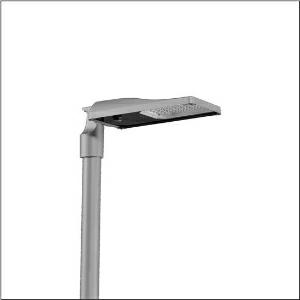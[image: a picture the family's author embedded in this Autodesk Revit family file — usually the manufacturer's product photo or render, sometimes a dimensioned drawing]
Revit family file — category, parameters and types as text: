
# Revit family: streetlight_sl_31_mini___st1_0a_5xh2d31r08ha_940f
name_source: partatom
category: Lighting Fixtures
units: mm (PartAtom-declared; Revit-internal decimal feet)

## family parameters
Cut with Voids When Loaded = No
Host = Face
Light Source = No
Part Type = Normal
Room Calculation Point = No
Round Connector Dimension = Use Diameter
Shared = No

## types (1)
- --- (1 x LED, 9230 lm, 68.3 W, 3000K)
    Apparent Load = 68 VA
    CIE Flux Codes = 37 72 97 100 100
    Color Rendering = 70
    Color Temperature = 3000K
    Default Elevation = 1800 mm
    Description = Streetlight SL 31 mini D4i, Desk-Remote mast luminaire for post-top, side-entry; light control with lens of PMMA; light distribution: ST1.0a, direct asymmetric distribution, for standard-compliant lighting for roads and squares; LED: luminous flux: 9.230lm, light colour: 730, colour temperature: 3000K; luminous efficacy: 135,1lm/W; control: pre-setting: logarithmic dimming characteristic, flexible luminous flux parameterisation, time-dependent luminous flux control, constant luminous flux control, power reduction, intelligent temperature release in ECG and LED module, overheat protection; luminaire housing, of diecast aluminium, Siteco® metallic grey (DB 702S), corrosivity category C5 high according to DIN EN ISO 12944; cover of toughened safety glass, transparent, mast flange of diecast aluminium, Siteco® metallic grey (DB 702S), spigot size: 76/60mm, mast flange included unmounted; with cable H07RN-F 2x 1.5mm², cable length: 8,5m, connection cable pre-assembled; mains connection: 220..240V, AC, 50/60Hz; power consumption (at start of service life): 68,3W / (at end of service life): 74,5W / (with reduced operation 50%): 29,5W; protection rating (complete): IP66; insulation class (complete): insulation class II (safety insulation); impact resistance: IK09; certification: CE, ENEC, ENEC+, VDE, UKCA, ZD4i; permissible operating ambient temperature for outdoor applications: -40..+50°C; packaging unit: 1 piece

Light Distribution: ST1.0a
    Height = 76 mm
    Lamp = 1 x LED
    Lamp Light Flux = 9230 lm
    Lamp Power = 68.3 W
    Lamp count = 1
    Length = 547 mm
    Luminous efficacy = 135 lm/W
    Manufacturer = Siteco
    ModVariant = No
    Model = 5XH2D31R08HA
    Number of Poles = 1
    OnlyDefault = Yes
    Power Factor = 1
    Product Name = Streetlight SL 31 mini | ST1.0a
    Product group = mast luminaire | pylon top
    ProductGroupID = 6100
    Protection Class = Protection class II
    Protection Degree = IP 66
    RLX_Detail_Level = 1
    RLX_Emergency_Light_Flux = 0 lm
    RLX_Emergency_Type = 0
    RLX_Emergency_Type_DB = No
    RlxData = <blob elided: 39393 chars, md5=d816b801>
    Socket = socket
    Standby Power = 0 W
    System Light Flux = 9230 lm
    System Power = 68 W
    Type Comments = factory setting: luminous flux: 100 % | dim-lin: 254 | 692 mA
    Type Image = l_1300328.jpg
    URL = http://relux.com
    VarID = @adj_019645
    Voltage = 0 V
    Weight = 0.00 kg
    Width = 265 mm

## geometry (parser evidence)
native form markers: Blend x4, Sweep x10
no freeform markers — native parametric forms only
